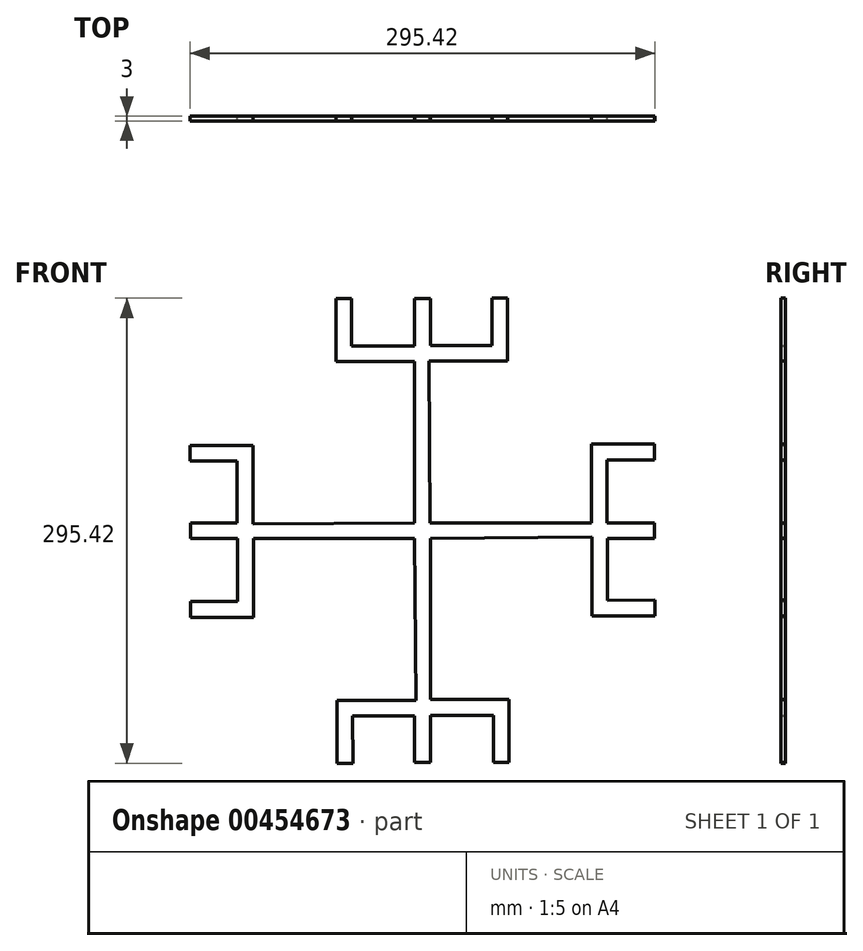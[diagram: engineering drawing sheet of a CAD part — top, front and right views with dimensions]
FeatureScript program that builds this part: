
annotation { "Feature Type Name" : "Feature", "Feature Type Description" : "" }
export const myFeature = defineFeature(function(context is Context, id is Id, definition is map)
    precondition{}
    {
        {
            var Q0;
            Q0=qCreatedBy(makeId("Front.planeOp"),FACE);
            var sketch = newSketch(context, id + "F0", { "sketchPlane" : qUnion([Q0])});
            skLineSegment(sketch, "E0", {"start": v(-5, 147.32) * mm, "end": v(5, 147.32) * mm});
            skLineSegment(sketch, "E1", {"start": v(4.36, 117.7) * mm, "end": v(44.36, 117.71) * mm});
            skLineSegment(sketch, "E2", {"start": v(44.36, 117.71) * mm, "end": v(44.12, 147.71) * mm});
            skLineSegment(sketch, "E3", {"start": v(4.12, 107.71) * mm, "end": v(54.12, 107.71) * mm});
            skLineSegment(sketch, "E4", {"start": v(54.12, 107.71) * mm, "end": v(54.12, 147.71) * mm});
            skLineSegment(sketch, "E5", {"start": v(54.12, 147.71) * mm, "end": v(44.12, 147.71) * mm});
            skLineSegment(sketch, "E6", {"start": v(-5, 107.32) * mm, "end": v(-55, 107.32) * mm});
            skLineSegment(sketch, "E7", {"start": v(-5, 117.32) * mm, "end": v(-45, 117.32) * mm});
            skLineSegment(sketch, "E8", {"start": v(-55, 107.32) * mm, "end": v(-55, 147.32) * mm});
            skLineSegment(sketch, "E9", {"start": v(-45, 117.32) * mm, "end": v(-45, 147.32) * mm});
            skLineSegment(sketch, "E10", {"start": v(-55, 147.32) * mm, "end": v(-45, 147.32) * mm});
            skLineSegment(sketch, "E11.trimOffspring", {"start": v(-5, 117.32) * mm, "end": v(-5, 147.32) * mm});
            skLineSegment(sketch, "E12.trimOffspring", {"start": v(5, 117.71) * mm, "end": v(5, 147.32) * mm});
            skLineSegment(sketch, "E13", {"start": v(-5, 107.32) * mm, "end": v(-5, 4.96) * mm});
            skLineSegment(sketch, "E14", {"start": v(4.12, 107.71) * mm, "end": v(4.96, 5) * mm});
            skLineSegment(sketch, "E15.1.0", {"start": v(-107.71, 4.12) * mm, "end": v(-5, 4.96) * mm});
            skLineSegment(sketch, "E15.1.1", {"start": v(-107.32, -5) * mm, "end": v(-4.96, -5) * mm});
            skLineSegment(sketch, "E15.1.2", {"start": v(-117.71, 5) * mm, "end": v(-147.32, 5) * mm});
            skLineSegment(sketch, "E15.1.3", {"start": v(-117.32, -5) * mm, "end": v(-147.32, -5) * mm});
            skLineSegment(sketch, "E15.1.4", {"start": v(-117.71, 44.36) * mm, "end": v(-147.71, 44.12) * mm});
            skLineSegment(sketch, "E15.1.5", {"start": v(-107.71, 54.12) * mm, "end": v(-147.71, 54.12) * mm});
            skLineSegment(sketch, "E15.1.6", {"start": v(-107.32, -55) * mm, "end": v(-147.32, -55) * mm});
            skLineSegment(sketch, "E15.1.7", {"start": v(-107.32, -5) * mm, "end": v(-107.32, -55) * mm});
            skLineSegment(sketch, "E15.1.8", {"start": v(-107.71, 4.12) * mm, "end": v(-107.71, 54.12) * mm});
            skLineSegment(sketch, "E15.1.9", {"start": v(-117.7, 4.36) * mm, "end": v(-117.71, 44.36) * mm});
            skLineSegment(sketch, "E15.1.10", {"start": v(-117.32, -5) * mm, "end": v(-117.32, -45) * mm});
            skLineSegment(sketch, "E15.1.11", {"start": v(-117.32, -45) * mm, "end": v(-147.32, -45) * mm});
            skLineSegment(sketch, "E15.1.12", {"start": v(-147.32, -5) * mm, "end": v(-147.32, 5) * mm});
            skLineSegment(sketch, "E15.1.13", {"start": v(-147.71, 54.12) * mm, "end": v(-147.71, 44.12) * mm});
            skLineSegment(sketch, "E15.1.15", {"start": v(-147.32, -55) * mm, "end": v(-147.32, -45) * mm});
            skLineSegment(sketch, "E15.2.0", {"start": v(-4.12, -107.71) * mm, "end": v(-4.96, -5) * mm});
            skLineSegment(sketch, "E15.2.1", {"start": v(5, -107.32) * mm, "end": v(5, -4.96) * mm});
            skLineSegment(sketch, "E15.2.2", {"start": v(-5, -117.71) * mm, "end": v(-5, -147.32) * mm});
            skLineSegment(sketch, "E15.2.3", {"start": v(5, -117.32) * mm, "end": v(5, -147.32) * mm});
            skLineSegment(sketch, "E15.2.4", {"start": v(-44.36, -117.71) * mm, "end": v(-44.12, -147.71) * mm});
            skLineSegment(sketch, "E15.2.5", {"start": v(-54.12, -107.71) * mm, "end": v(-54.12, -147.71) * mm});
            skLineSegment(sketch, "E15.2.6", {"start": v(55, -107.32) * mm, "end": v(55, -147.32) * mm});
            skLineSegment(sketch, "E15.2.7", {"start": v(5, -107.32) * mm, "end": v(55, -107.32) * mm});
            skLineSegment(sketch, "E15.2.8", {"start": v(-4.12, -107.71) * mm, "end": v(-54.12, -107.71) * mm});
            skLineSegment(sketch, "E15.2.9", {"start": v(-4.36, -117.7) * mm, "end": v(-44.36, -117.71) * mm});
            skLineSegment(sketch, "E15.2.10", {"start": v(5, -117.32) * mm, "end": v(45, -117.32) * mm});
            skLineSegment(sketch, "E15.2.11", {"start": v(45, -117.32) * mm, "end": v(45, -147.32) * mm});
            skLineSegment(sketch, "E15.2.12", {"start": v(5, -147.32) * mm, "end": v(-5, -147.32) * mm});
            skLineSegment(sketch, "E15.2.13", {"start": v(-54.12, -147.71) * mm, "end": v(-44.12, -147.71) * mm});
            skLineSegment(sketch, "E15.2.14", {"start": v(-5, 0) * mm, "end": v(5, 0) * mm});
            skLineSegment(sketch, "E15.2.15", {"start": v(55, -147.32) * mm, "end": v(45, -147.32) * mm});
            skLineSegment(sketch, "E15.3.0", {"start": v(107.71, -4.12) * mm, "end": v(5, -4.96) * mm});
            skLineSegment(sketch, "E15.3.1", {"start": v(107.32, 5) * mm, "end": v(4.96, 5) * mm});
            skLineSegment(sketch, "E15.3.2", {"start": v(117.71, -5) * mm, "end": v(147.32, -5) * mm});
            skLineSegment(sketch, "E15.3.3", {"start": v(117.32, 5) * mm, "end": v(147.32, 5) * mm});
            skLineSegment(sketch, "E15.3.4", {"start": v(117.71, -44.36) * mm, "end": v(147.71, -44.12) * mm});
            skLineSegment(sketch, "E15.3.5", {"start": v(107.71, -54.12) * mm, "end": v(147.71, -54.12) * mm});
            skLineSegment(sketch, "E15.3.6", {"start": v(107.32, 55) * mm, "end": v(147.32, 55) * mm});
            skLineSegment(sketch, "E15.3.7", {"start": v(107.32, 5) * mm, "end": v(107.32, 55) * mm});
            skLineSegment(sketch, "E15.3.8", {"start": v(107.71, -4.12) * mm, "end": v(107.71, -54.12) * mm});
            skLineSegment(sketch, "E15.3.9", {"start": v(117.7, -4.36) * mm, "end": v(117.71, -44.36) * mm});
            skLineSegment(sketch, "E15.3.10", {"start": v(117.32, 5) * mm, "end": v(117.32, 45) * mm});
            skLineSegment(sketch, "E15.3.11", {"start": v(117.32, 45) * mm, "end": v(147.32, 45) * mm});
            skLineSegment(sketch, "E15.3.12", {"start": v(147.32, 5) * mm, "end": v(147.32, -5) * mm});
            skLineSegment(sketch, "E15.3.13", {"start": v(147.71, -54.12) * mm, "end": v(147.71, -44.12) * mm});
            skLineSegment(sketch, "E15.3.15", {"start": v(147.32, 55) * mm, "end": v(147.32, 45) * mm});
            skPoint(sketch, "E15.center", {"position": v(0, 0) * mm});
            skPoint(sketch, "E16.orphan", {"position": v(0, 5) * mm});
            skPoint(sketch, "E17.orphan", {"position": v(5, 0) * mm});
            skPoint(sketch, "E18.orphan", {"position": v(-5, 0) * mm});
            skPoint(sketch, "E19.orphan", {"position": v(0, -5) * mm});
            skSolve(sketch);
        }
        {
            var Q0;
            Q0 = qSketchRegion(id + "F0", true);
            extrude(context, id + "F1", {"entities" : qUnion([Q0]), "depth" : 3 * mm, "offsetDistance" : 25 * mm});
        }
    });
